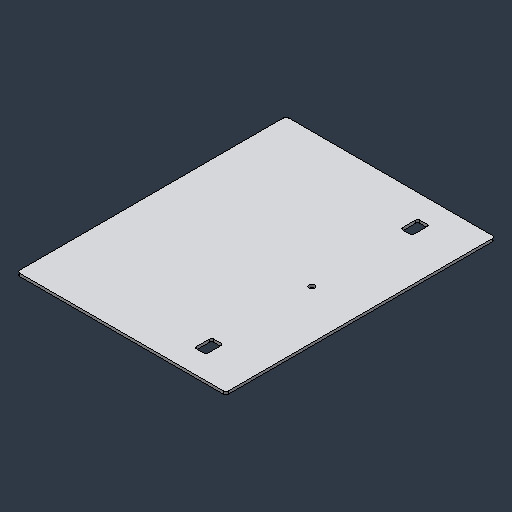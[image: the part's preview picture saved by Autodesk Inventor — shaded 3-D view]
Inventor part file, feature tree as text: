
AUTODESK INVENTOR PART (.ipt)
format: ipt  version: 2024.3 (Build 283343000, 343)  size: 92,160 bytes
history: native  units: mm (DEFAULTED — no unit token found)
features: fillet x1
ambient origin geometry x8: Origin, YZ Plane, XZ Plane, XY Plane, X Axis, Y Axis, Z Axis, Center Point
bodies: Solid1 (feature_tree)
feature tree (1):
  fillet  "Fillet2"  [1 undecoded]
note: 1 required parameter value undecoded (feature->parameter linkage not recoverable at this tier; creation-order binding heuristic only, values carry confidence <= 0.55)
